# Revit family: Storage-Mounted-Teknion-BRHG-Tower_Full_Glass_Doors_High_Secondary_Desk-R2015
name_source: partatom
category: Furniture
revit_build: Autodesk Revit Architecture 2015 (Build: 20140323_1530(x64)
units: mm (PartAtom-declared; Revit-internal decimal feet)

## types (2) — shared parameters
Assembly Code = E2020200
Manufacturer = Teknion
Manufacturer Fax = 416.661.4586
Part Number = BRHG
Product Documentation Link = http://www.teknion.com
Product Line = Expansion Casegoods
Product Page URL = http://www.teknion.com
Series = Expansion Casegoods
Sustainability Data = http://www.teknion.com
URL = www.teknion.com
Unit Weight URL = http://www.teknion.com
Warranty = http://www.teknion.com

## per-type parameters (varying)
| type | Actual Height | Description | Height | Model | Top Shelf Vertical Offset |
| 18"d x 18"w x 66"h | 65.165 " | Tower with Full Glass Door – High Secondary Desk Mounted, 18"d, 18"w, 66"h | 66 " | BRHGS181866 | 14.906 " |
| 18"d x 18"w x 72"h | 71.406 " | Tower with Full Glass Door – High Secondary Desk Mounted, 18"d, 18"w, 72"h | 72 " | BRHGS181872 | 16.986 " |

## geometry (parser evidence)
native form markers: Blend x152, Sweep x3
no freeform markers — native parametric forms only
